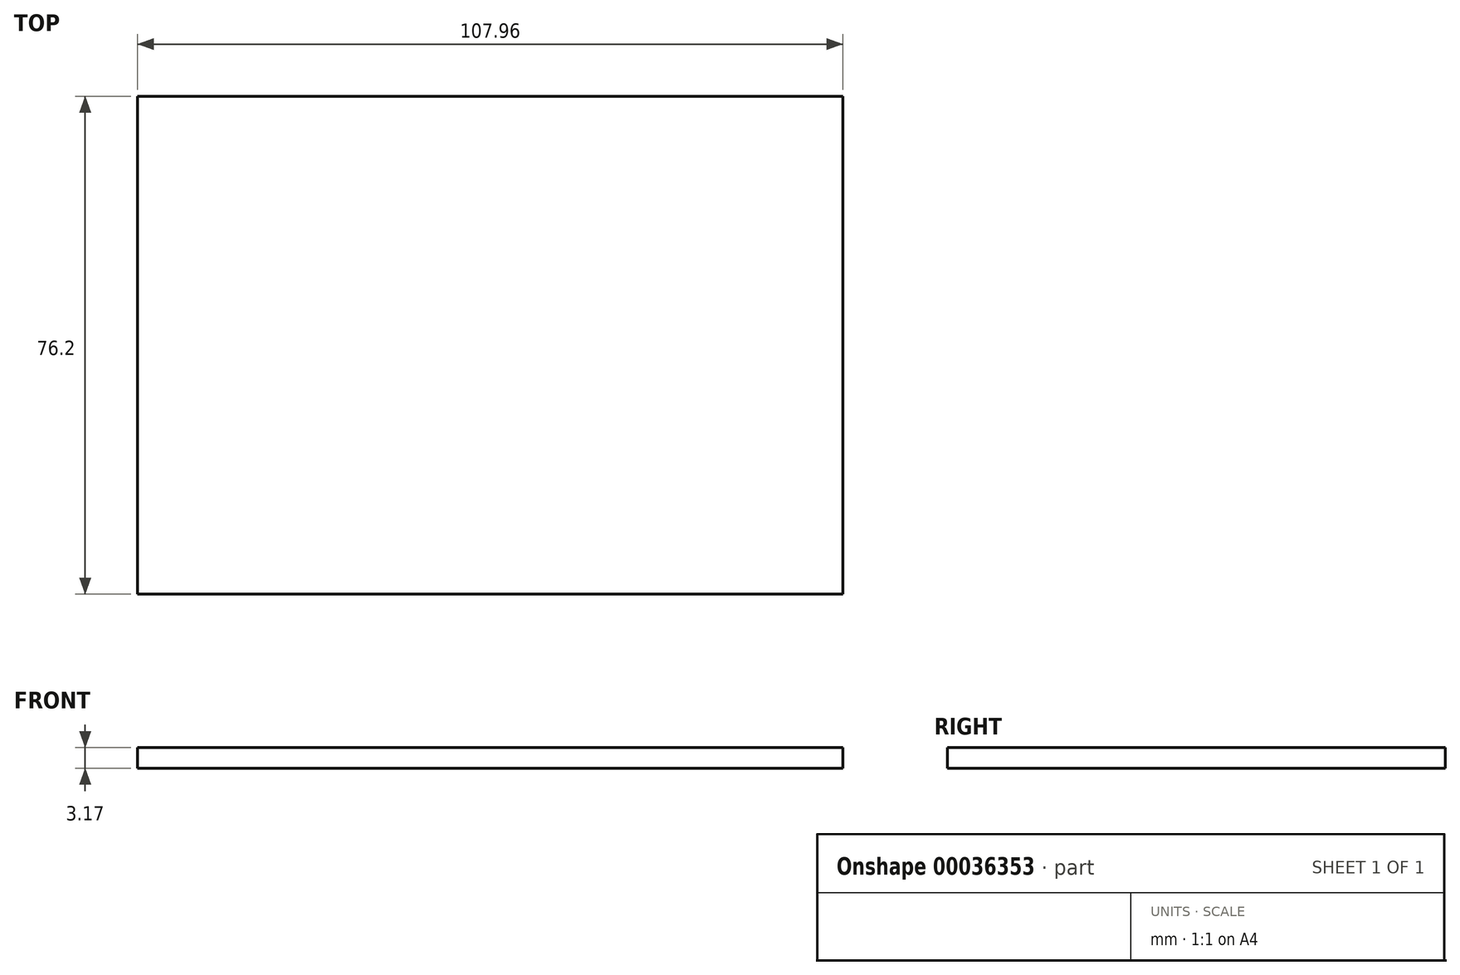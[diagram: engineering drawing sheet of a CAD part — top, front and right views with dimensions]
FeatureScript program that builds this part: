
annotation { "Feature Type Name" : "Feature", "Feature Type Description" : "" }
export const myFeature = defineFeature(function(context is Context, id is Id, definition is map)
    precondition{}
    {
        {
            var Q0;
            Q0=qCreatedBy(makeId("Top.planeOp"),FACE);
            var sketch = newSketch(context, id + "F0", { "sketchPlane" : qUnion([Q0])});
            skLineSegment(sketch, "E0.rect.bottom", {"start": v(-53.97, 38.1) * mm, "end": v(53.98, 38.1) * mm});
            skLineSegment(sketch, "E0.rect.top", {"start": v(-53.98, -38.1) * mm, "end": v(53.97, -38.1) * mm});
            skLineSegment(sketch, "E0.rect.left", {"start": v(-53.97, 38.1) * mm, "end": v(-53.98, -38.1) * mm});
            skLineSegment(sketch, "E0.rect.right", {"start": v(53.98, 38.1) * mm, "end": v(53.97, -38.1) * mm});
            skPoint(sketch, "E0.rect.middle", {"position": v(0, 0) * mm});
            skSolve(sketch);
        }
        {
            var Q0;
            Q0=makeQuery(id+"F0.imprint","IMPRINT",FACE,{"disambiguationData":[TD([[makeQuery(id+"F0.imprint","IMPRINT",EDGE,{"derivedFrom":sQuery(id+"F0.wireOp",EDGE,"E0.rect.bottom")}),-1.0]])]});
            extrude(context, id + "F1", {"entities" : qUnion([Q0]), "depth" : 3.17 * mm});
        }
    });
